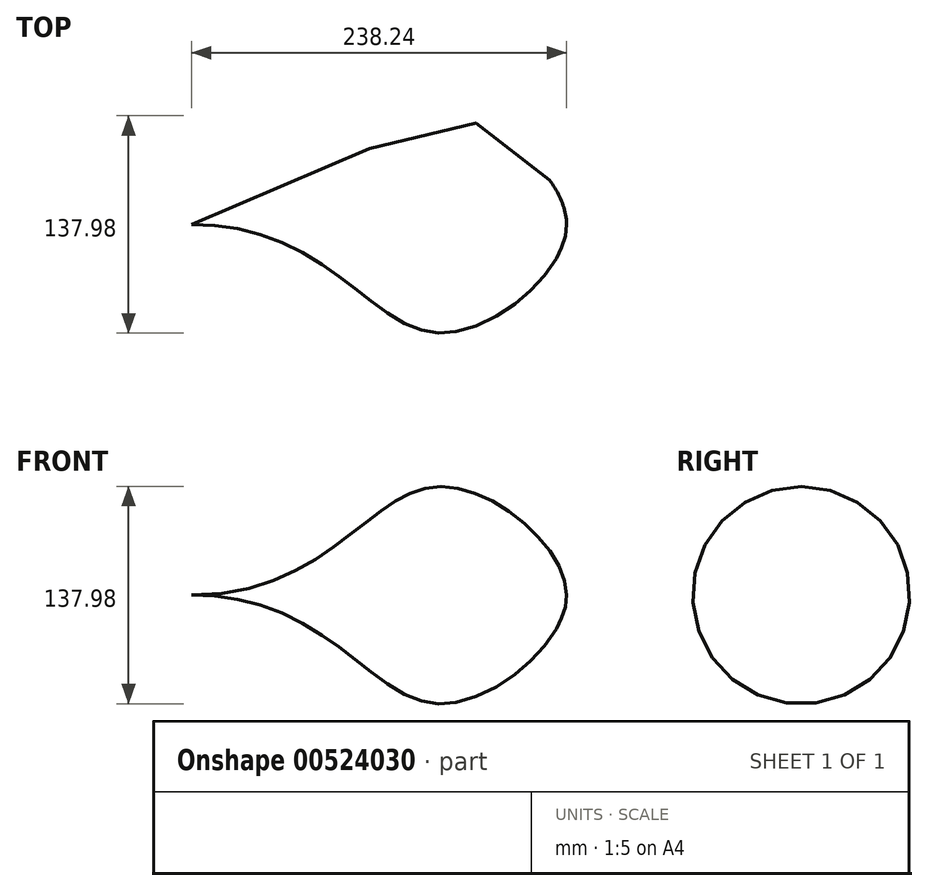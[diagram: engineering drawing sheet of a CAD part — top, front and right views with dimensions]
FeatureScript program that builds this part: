
annotation { "Feature Type Name" : "Feature", "Feature Type Description" : "" }
export const myFeature = defineFeature(function(context is Context, id is Id, definition is map)
    precondition{}
    {
        {
            var Q0;
            Q0=qCreatedBy(makeId("Front.planeOp"),FACE);
            var sketch = newSketch(context, id + "F0", { "sketchPlane" : qUnion([Q0])});
            skFitSpline(sketch, "E0", {"points": [v(0, 0) * mm, v(157.08, 68.96) * mm, v(238.24, 0) * mm], "startDerivative": vector(469.29, 0) * mm, "endDerivative": vector(0, -204.56) * mm});
            skLineSegment(sketch, "E1", {"start": v(0, 0) * mm, "end": v(238.24, 0) * mm});
            skSolve(sketch);
        }
        {
            var Q0;
            Q0=makeQuery(id+"F0.imprint","IMPRINT",FACE,{"disambiguationData":[TD([[makeQuery(id+"F0.imprint","IMPRINT",EDGE,{"derivedFrom":sQuery(id+"F0.wireOp",EDGE,"E0")}),-1.0]])]});
            var Q1;
            Q1=sQuery(id+"F0.wireOp",EDGE,"E1");
            revolve(context, id + "F1", {"entities" : qUnion([Q0]), "axis" : qUnion([Q1]), "revolveType" : RevolveType.FULL});
        }
    });
